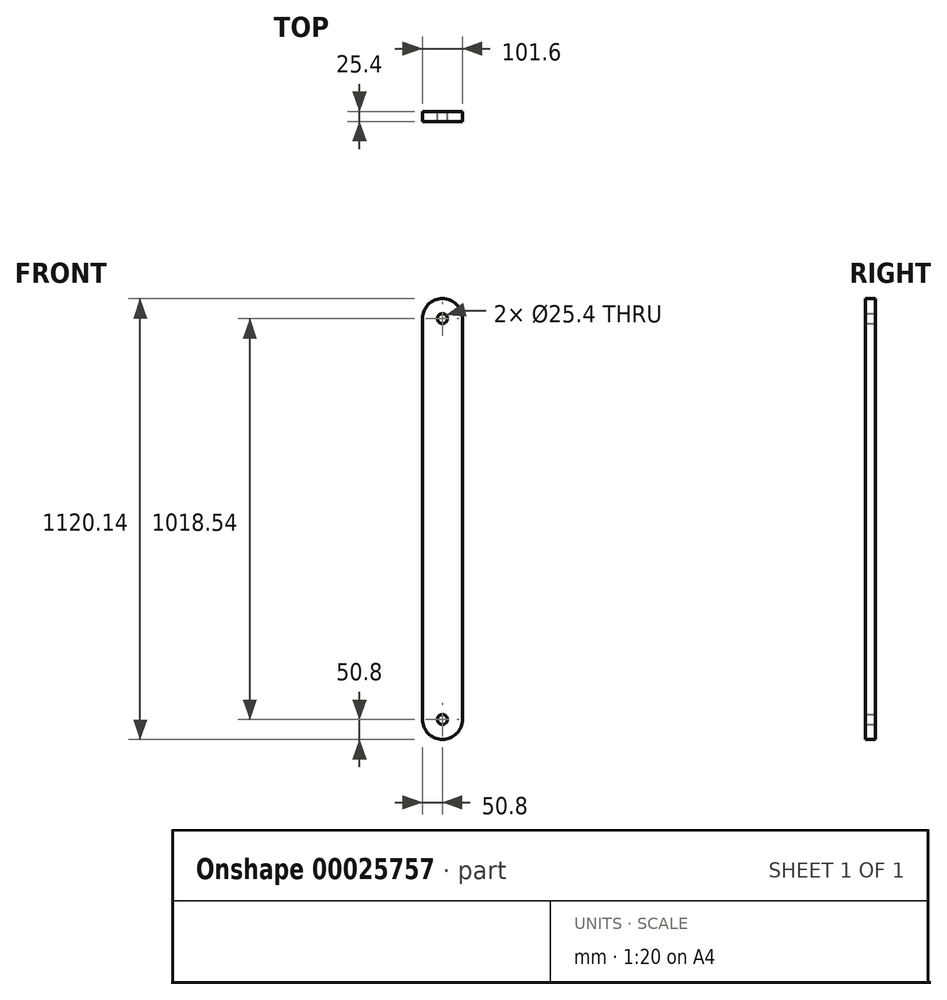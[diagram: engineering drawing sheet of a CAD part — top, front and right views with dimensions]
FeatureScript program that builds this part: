
annotation { "Feature Type Name" : "Feature", "Feature Type Description" : "" }
export const myFeature = defineFeature(function(context is Context, id is Id, definition is map)
    precondition{}
    {
        {
            var Q0;
            Q0=qCreatedBy(makeId("Front.planeOp"),FACE);
            var sketch = newSketch(context, id + "F0", { "sketchPlane" : qUnion([Q0])});
            skLineSegment(sketch, "E0", {"start": v(0, 0) * mm, "end": v(0, 1018.54) * mm});
            skLineSegment(sketch, "E1", {"start": v(-101.6, 0) * mm, "end": v(-101.6, 1018.54) * mm});
            skArc(sketch, "E2", {"start": v(0, 1018.54) * mm, "mid": v(-50.8, 1069.34) * mm, "end": v(-101.6, 1018.54) * mm});
            skArc(sketch, "E3", {"start": v(-101.6, 0) * mm, "mid": v(-50.8, -50.8) * mm, "end": v(0, 0) * mm});
            skCircle(sketch, "E4", {"center": v(-50.8, 0) * mm, "radius": 12.7 * mm});
            skCircle(sketch, "E5", {"center": v(-50.8, 1018.54) * mm, "radius": 12.7 * mm});
            skSolve(sketch);
        }
        {
            var Q0;
            Q0 = qSketchRegion(id + "F0", true);
            extrude(context, id + "F1", {"entities" : qUnion([Q0]), "depth" : 25.4 * mm});
        }
    });
